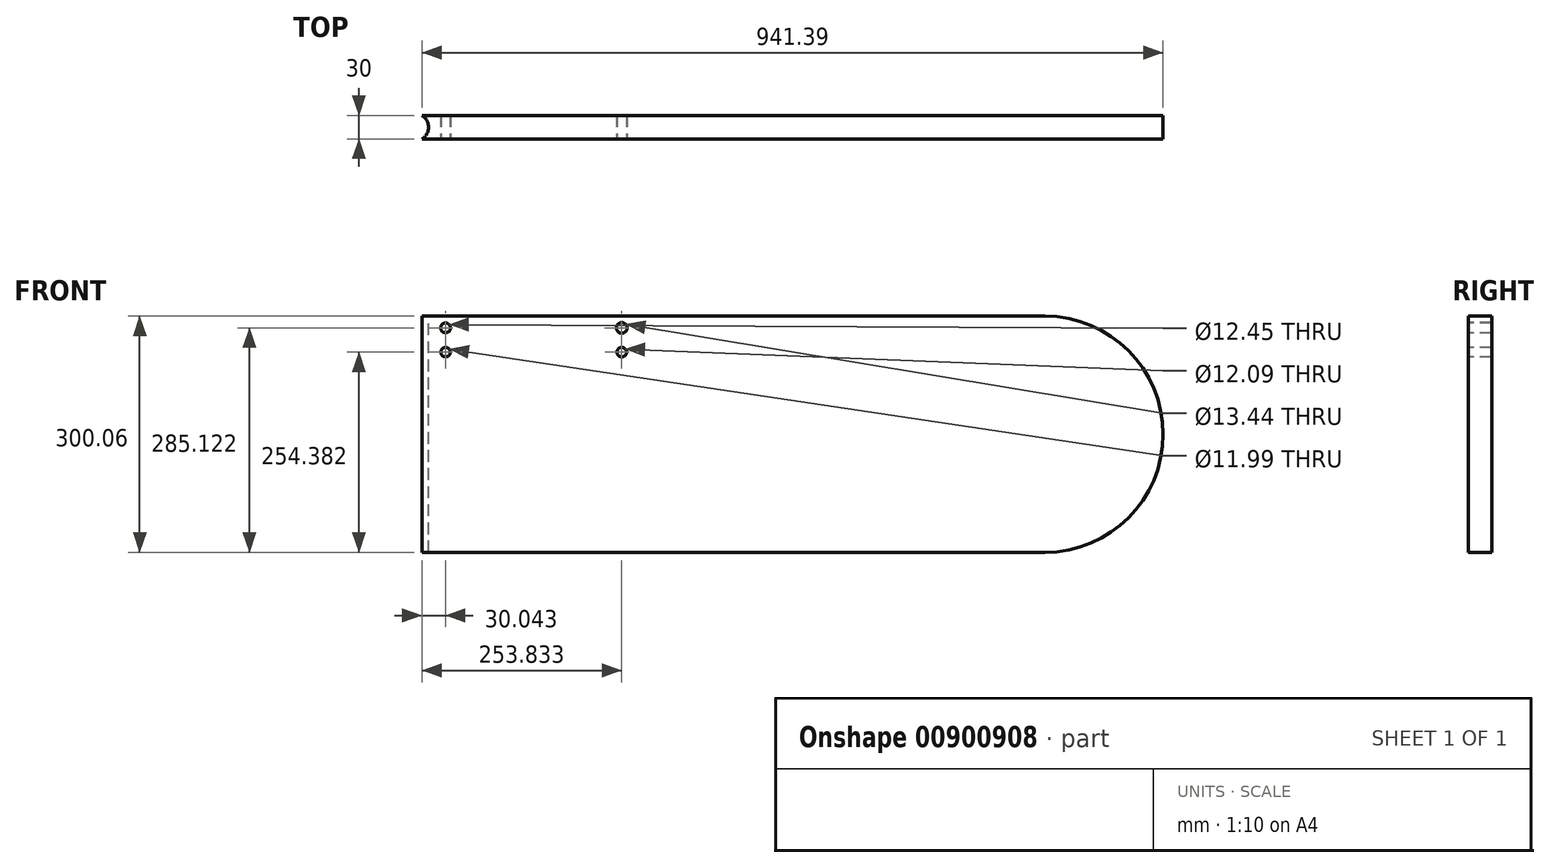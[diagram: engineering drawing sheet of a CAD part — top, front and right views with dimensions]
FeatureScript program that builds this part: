
annotation { "Feature Type Name" : "Feature", "Feature Type Description" : "" }
export const myFeature = defineFeature(function(context is Context, id is Id, definition is map)
    precondition{}
    {
        {
            var Q0;
            Q0=qCreatedBy(makeId("Front.planeOp"),FACE);
            var sketch = newSketch(context, id + "F0", { "sketchPlane" : qUnion([Q0])});
            skLineSegment(sketch, "E0.bottom", {"start": v(400.26, -150.03) * mm, "end": v(-400.26, -150.03) * mm});
            skLineSegment(sketch, "E0.top", {"start": v(400.26, 150.03) * mm, "end": v(-400.26, 150.03) * mm});
            skLineSegment(sketch, "E0.right", {"start": v(-400.26, -150.03) * mm, "end": v(-400.26, 150.03) * mm});
            skPoint(sketch, "E0.middle", {"position": v(0, 0) * mm});
            skArc(sketch, "E1", {"start": v(400.26, -150.03) * mm, "mid": v(550.29, 0) * mm, "end": v(400.26, 150.03) * mm});
            skSolve(sketch);
        }
        {
            var Q0;
            Q0 = qSketchRegion(id + "F0", true);
            extrude(context, id + "F1", {"entities" : qUnion([Q0]), "depth" : 30 * mm, "offsetDistance" : 25 * mm});
        }
        {
            var Q0;
            Q0=makeQuery(id+"F1.opExtrude","CAP_FACE",FACE,{"disambiguationData":[OSD([sQuery(id+"F0.wireOp",EDGE,"E0.bottom"),sQuery(id+"F0.wireOp",EDGE,"E0.top"),sQuery(id+"F0.wireOp",EDGE,"E0.right"),sQuery(id+"F0.wireOp",EDGE,"E1")])],"isStart":false});
            var sketch = newSketch(context, id + "F2", { "sketchPlane" : qUnion([Q0])});
            skCircle(sketch, "E2", {"center": v(-361.06, 135.1) * mm, "radius": 6.22 * mm});
            skPoint(sketch, "E3.end.orphan", {"position": v(-297.85, 135.1) * mm});
            skPoint(sketch, "E4.orphan", {"position": v(-400.26, 135.1) * mm});
            skCircle(sketch, "E5", {"center": v(-361.06, 104.35) * mm, "radius": 6 * mm});
            skCircle(sketch, "E6", {"center": v(-137.27, 135.1) * mm, "radius": 6.72 * mm});
            skCircle(sketch, "E7", {"center": v(-137.27, 104.35) * mm, "radius": 6.04 * mm});
            skSolve(sketch);
        }
        {
            var Q0;
            Q0 = qSketchRegion(id + "F2", true);
            extrude(context, id + "F3", {"entities" : qUnion([Q0]), "operationType" : NewBodyOperationType.REMOVE, "oppositeDirection" : true, "depth" : 35 * mm, "offsetDistance" : 25 * mm});
        }
        {
            var Q0;
            Q0=qCreatedBy(makeId("Top.planeOp"),FACE);
            var sketch = newSketch(context, id + "F4", { "sketchPlane" : qUnion([Q0])});
            skLineSegment(sketch, "E8", {"start": v(-400.2, -30) * mm, "end": v(-400.2, 0) * mm});
            skCircle(sketch, "E9", {"center": v(-400.2, -15) * mm, "radius": 17.54 * mm});
            skSolve(sketch);
        }
        {
            var Q0;
            Q0 = qSketchRegion(id + "F4", true);
            extrude(context, id + "F5", {"entities" : qUnion([Q0]), "operationType" : NewBodyOperationType.REMOVE, "endBound" : BoundingType.SYMMETRIC, "oppositeDirection" : true, "depth" : 1000 * mm, "offsetDistance" : 25 * mm});
        }
    });
